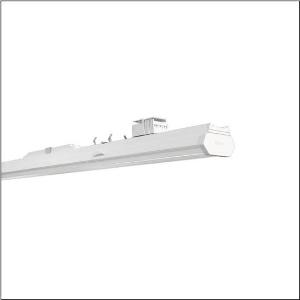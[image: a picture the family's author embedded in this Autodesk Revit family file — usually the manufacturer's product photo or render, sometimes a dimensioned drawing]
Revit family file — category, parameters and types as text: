
# Revit family: licross_21_protected_mo_52tp12dn4axg
name_source: partatom
category: Lighting Fixtures
units: mm (PartAtom-declared; Revit-internal decimal feet)

## family parameters
Cut with Voids When Loaded = No
Host = Face
Light Source = No
Part Type = Normal
Room Calculation Point = No
Round Connector Dimension = Use Diameter
Shared = No

## types (1)
- --- (1 x LED, 10000 lm, 57.5 W, 4000K)
    Apparent Load = 58 VA
    CIE Flux Codes = 73 92 98 99 100
    Color Rendering = 80
    Color Temperature = 4000K
    Default Elevation = 1800 mm
    Description = Licross 21 Protected MO, luminaire insert, of sheet steel, galvanised, coil coated, white, length: 1.500mm, width: 90mm, height: 103mm, LED rated luminous flux: 10.000lm, light colour: 840, SDCM (Standard Deviation of Colour Matching)MacAdam ≤ 3 SDCM (initial), control gear: DALI 2, with plug, 5-pole, with phase selection, mains connection: 220..240V, AC, 50/60Hz, rated input power: 58W, internal wiring halogen-free, primary light control with lens, of plastic, primary optical cover: cover, of PMMA, light emission: direct distribution, primary light characteristic: symmetric, protection rating (complete): IP64, insulation class (complete): insulation class I (protective earthing), certification: CE, ENEC, VDE, UKCA, protection symbol: D if used in an environment with conductive dust loads with corresponding accessories, impact resistance: IK06, permissible ambient temperature for indoor applications: -25..+40°C, corresponds to IFS (International Featured Standards) requirements for safety and quality in the food industry, reducing of maximum allowable ambient temperature of 5°C with ceiling mounting, LABS conformity tested according to VDMA 24364:2018-05, The light source and the operating device comply with the requirements of the Ecodesign Regulation (EU) 2019/2020 and are replaceable in accordance with this regulation, packaging unit: 1 piece
    Height = 92 mm
    Lamp = 1 x LED
    Lamp Light Flux = 10000 lm
    Lamp Power = 57.5 W
    Lamp count = 1
    Length = 1500 mm
    Luminous efficacy = 174 lm/W
    Manufacturer = Siteco
    ModVariant = No
    Model = 52TP12DN4AXG
    Mounting Place = Ceiling
    Mounting Type = Pendant
    Number of Poles = 1
    OnlyDefault = Yes
    Power Factor = 1
    Product Name = Licross 21 Protected MO
    Product group = luminaire insert | ceiling pendant
    ProductGroupID = 901
    Protection Class = Protection class I
    Protection Degree = IP 64
    RLX_Detail_Level = 1
    RLX_Emergency_Light_Flux = 0 lm
    RLX_Emergency_Type = 0
    RLX_Emergency_Type_DB = No
    RlxData = <blob elided: 24677 chars, md5=725fd9eb>
    Socket = socket
    Standby Power = 0 W
    System Light Flux = 10000 lm
    System Power = 58 W
    Type Comments = factory setting: luminous flux: 100 % | dim-lin: 254 | 388 mA
    Type Image = l_1256148.jpg
    URL = http://relux.com
    VarID = @adj_130317
    Voltage = 0 V
    Weight = 0.00 kg
    Width = 88 mm

## geometry (parser evidence)
native form markers: Blend x4, Sweep x10
no freeform markers — native parametric forms only
